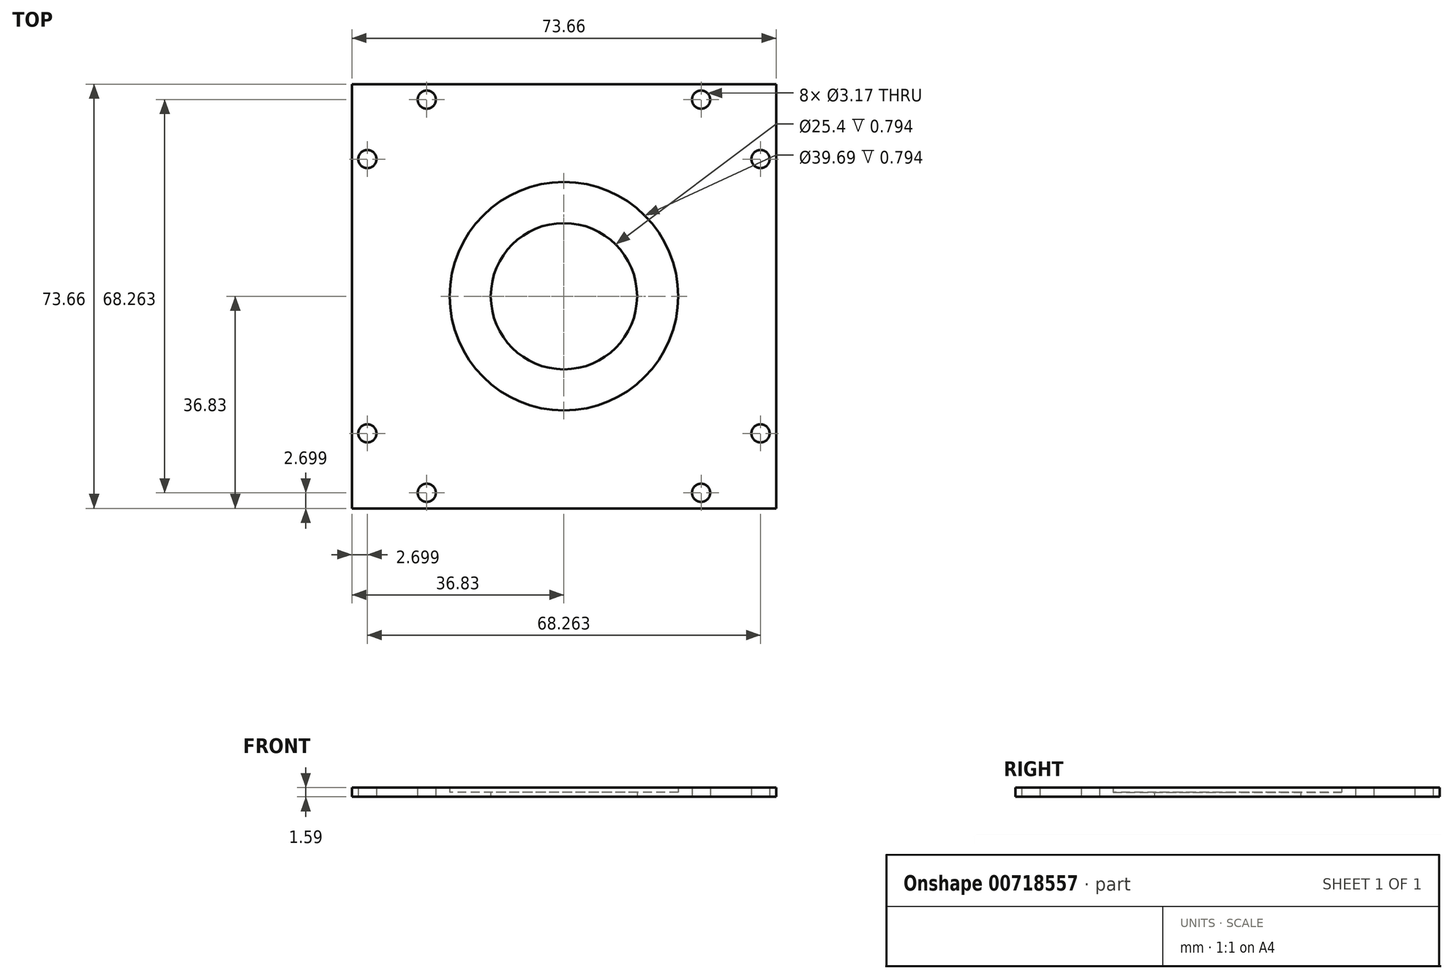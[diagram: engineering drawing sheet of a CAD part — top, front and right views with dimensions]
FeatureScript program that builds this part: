
annotation { "Feature Type Name" : "Feature", "Feature Type Description" : "" }
export const myFeature = defineFeature(function(context is Context, id is Id, definition is map)
    precondition{}
    {
        {
            var Q0;
            Q0=qCreatedBy(makeId("Top.planeOp"),FACE);
            var sketch = newSketch(context, id + "F0", { "sketchPlane" : qUnion([Q0])});
            skPoint(sketch, "E0.middle", {"position": v(0, 0) * mm});
            skCircle(sketch, "E1", {"center": v(0, 0) * mm, "radius": 12.7 * mm});
            skCircle(sketch, "E2", {"center": v(0, 0) * mm, "radius": 19.84 * mm});
            skCircle(sketch, "E3", {"center": v(-23.81, 34.13) * mm, "radius": 1.59 * mm});
            skLineSegment(sketch, "E4.bottom", {"start": v(-36.83, 36.83) * mm, "end": v(36.83, 36.83) * mm});
            skLineSegment(sketch, "E4.top", {"start": v(-36.83, -36.83) * mm, "end": v(36.83, -36.83) * mm});
            skLineSegment(sketch, "E4.left", {"start": v(-36.83, 36.83) * mm, "end": v(-36.83, -36.83) * mm});
            skLineSegment(sketch, "E4.right", {"start": v(36.83, 36.83) * mm, "end": v(36.83, -36.83) * mm});
            skCircle(sketch, "E5", {"center": v(-23.81, -34.13) * mm, "radius": 1.59 * mm});
            skCircle(sketch, "E6", {"center": v(23.81, -34.13) * mm, "radius": 1.59 * mm});
            skCircle(sketch, "E7", {"center": v(23.81, 34.13) * mm, "radius": 1.59 * mm});
            skCircle(sketch, "E8", {"center": v(-34.13, 23.81) * mm, "radius": 1.59 * mm});
            skCircle(sketch, "E9", {"center": v(-34.13, -23.81) * mm, "radius": 1.59 * mm});
            skCircle(sketch, "E10", {"center": v(34.13, -23.81) * mm, "radius": 1.59 * mm});
            skCircle(sketch, "E11", {"center": v(34.13, 23.81) * mm, "radius": 1.59 * mm});
            skSolve(sketch);
        }
        {
            var Q0;
            Q0=makeQuery(id+"F0.imprint","IMPRINT",FACE,{"disambiguationData":[TD([[makeQuery(id+"F0.imprint","IMPRINT",EDGE,{"derivedFrom":sQuery(id+"F0.wireOp",EDGE,"E1")}),-1.0]])]});
            extrude(context, id + "F1", {"entities" : qUnion([Q0]), "depth" : 0.8 * mm, "offsetDistance" : 25.4 * mm});
        }
        {
            var Q0;
            Q0=makeQuery(id+"F0.imprint","IMPRINT",FACE,{"disambiguationData":[TD([[makeQuery(id+"F0.imprint","IMPRINT",EDGE,{"derivedFrom":sQuery(id+"F0.wireOp",EDGE,"E2")}),-1.0]])]});
            extrude(context, id + "F2", {"entities" : qUnion([Q0]), "operationType" : NewBodyOperationType.ADD, "depth" : 1.59 * mm, "offsetDistance" : 25.4 * mm});
        }
    });
